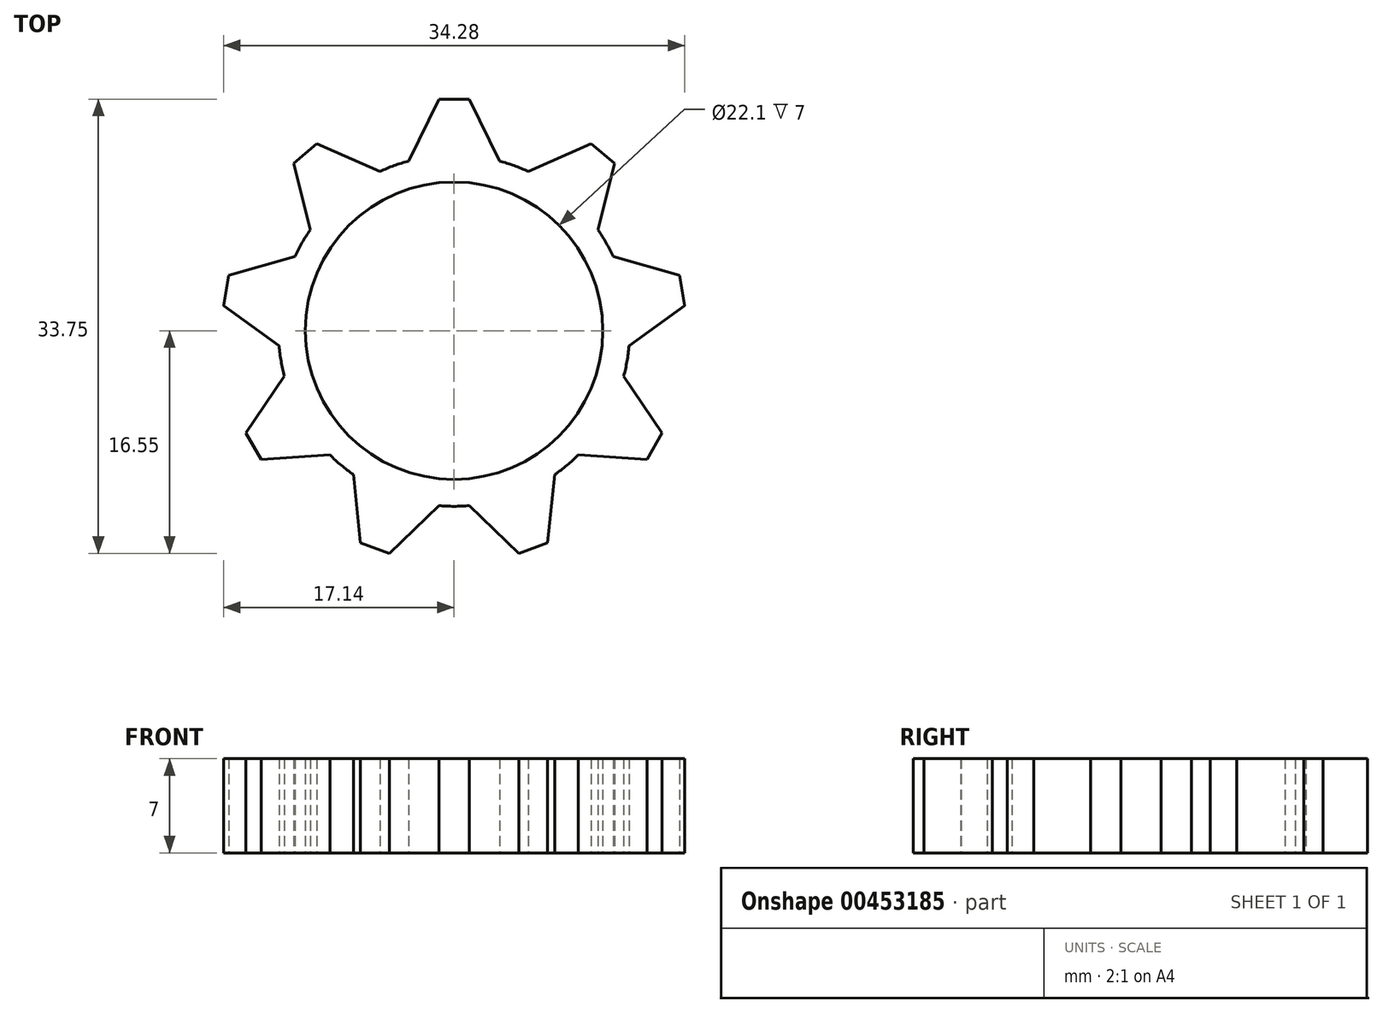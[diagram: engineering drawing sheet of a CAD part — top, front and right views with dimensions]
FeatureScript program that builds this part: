
annotation { "Feature Type Name" : "Feature", "Feature Type Description" : "" }
export const myFeature = defineFeature(function(context is Context, id is Id, definition is map)
    precondition{}
    {
        {
            var Q0;
            Q0=qCreatedBy(makeId("Top.planeOp"),FACE);
            var sketch = newSketch(context, id + "F0", { "sketchPlane" : qUnion([Q0])});
            skCircle(sketch, "E0", {"center": v(0, 0) * mm, "radius": 11.05 * mm});
            skCircle(sketch, "E1.0", {"center": v(0, 0) * mm, "radius": 13.05 * mm});
            skPoint(sketch, "E2.orphan", {"position": v(3.38, 12.6) * mm});
            skPoint(sketch, "E3.MirrorCS.end.orphan", {"position": v(-3.38, 12.6) * mm});
            skPoint(sketch, "E4.1.0", {"position": v(11.37, 6.69) * mm});
            skPoint(sketch, "E4.1.1", {"position": v(6.58, 11.46) * mm});
            skPoint(sketch, "E4.2.0", {"position": v(12.86, -3.14) * mm});
            skPoint(sketch, "E4.2.1", {"position": v(12.83, 3.61) * mm});
            skPoint(sketch, "E4.3.0", {"position": v(6.97, -11.16) * mm});
            skPoint(sketch, "E4.3.1", {"position": v(11.72, -6.35) * mm});
            skPoint(sketch, "E4.4.0", {"position": v(-2.86, -12.68) * mm});
            skPoint(sketch, "E4.4.1", {"position": v(3.9, -12.63) * mm});
            skPoint(sketch, "E4.5.0", {"position": v(-10.9, -6.82) * mm});
            skPoint(sketch, "E4.5.1", {"position": v(-6.08, -11.55) * mm});
            skPoint(sketch, "E4.6.0", {"position": v(-12.45, 3) * mm});
            skPoint(sketch, "E4.6.1", {"position": v(-12.38, -3.75) * mm});
            skPoint(sketch, "E4.7.0", {"position": v(-6.62, 11.06) * mm});
            skPoint(sketch, "E4.7.1", {"position": v(-11.33, 6.22) * mm});
            skPoint(sketch, "E4.center", {"position": v(0.21, -0.02) * mm});
            skLineSegment(sketch, "E5", {"start": v(0, 17.2) * mm, "end": v(1.14, 17.2) * mm});
            skLineSegment(sketch, "E6.MirrorCS", {"start": v(0, 17.2) * mm, "end": v(-1.14, 17.2) * mm});
            skLineSegment(sketch, "E7", {"start": v(-3.38, 12.6) * mm, "end": v(-1.13, 17.2) * mm});
            skLineSegment(sketch, "E8", {"start": v(1.13, 17.2) * mm, "end": v(3.38, 12.6) * mm});
            skLineSegment(sketch, "E9.1.0", {"start": v(-10.19, 13.9) * mm, "end": v(-5.52, 11.83) * mm});
            skLineSegment(sketch, "E9.1.1", {"start": v(-11.06, 13.18) * mm, "end": v(-10.19, 13.9) * mm});
            skLineSegment(sketch, "E9.1.2", {"start": v(-11.06, 13.18) * mm, "end": v(-11.93, 12.45) * mm});
            skLineSegment(sketch, "E9.1.3", {"start": v(-10.69, 7.49) * mm, "end": v(-11.93, 12.45) * mm});
            skLineSegment(sketch, "E9.2.0", {"start": v(-16.74, 4.1) * mm, "end": v(-11.83, 5.52) * mm});
            skLineSegment(sketch, "E9.2.1", {"start": v(-16.94, 2.99) * mm, "end": v(-16.74, 4.1) * mm});
            skLineSegment(sketch, "E9.2.2", {"start": v(-16.94, 2.99) * mm, "end": v(-17.14, 1.87) * mm});
            skLineSegment(sketch, "E9.2.3", {"start": v(-13, -1.14) * mm, "end": v(-17.14, 1.87) * mm});
            skLineSegment(sketch, "E9.3.0", {"start": v(-15.46, -7.62) * mm, "end": v(-12.6, -3.38) * mm});
            skLineSegment(sketch, "E9.3.1", {"start": v(-14.9, -8.6) * mm, "end": v(-15.46, -7.62) * mm});
            skLineSegment(sketch, "E9.3.2", {"start": v(-14.9, -8.6) * mm, "end": v(-14.33, -9.58) * mm});
            skLineSegment(sketch, "E9.3.3", {"start": v(-9.23, -9.23) * mm, "end": v(-14.33, -9.58) * mm});
            skLineSegment(sketch, "E9.4.0", {"start": v(-6.95, -15.77) * mm, "end": v(-7.49, -10.69) * mm});
            skLineSegment(sketch, "E9.4.1", {"start": v(-5.88, -16.16) * mm, "end": v(-6.95, -15.77) * mm});
            skLineSegment(sketch, "E9.4.2", {"start": v(-5.88, -16.16) * mm, "end": v(-4.82, -16.55) * mm});
            skLineSegment(sketch, "E9.4.3", {"start": v(-1.14, -13) * mm, "end": v(-4.82, -16.55) * mm});
            skLineSegment(sketch, "E9.5.0", {"start": v(4.82, -16.55) * mm, "end": v(1.14, -13) * mm});
            skLineSegment(sketch, "E9.5.1", {"start": v(5.88, -16.16) * mm, "end": v(4.82, -16.55) * mm});
            skLineSegment(sketch, "E9.5.2", {"start": v(5.88, -16.16) * mm, "end": v(6.95, -15.77) * mm});
            skLineSegment(sketch, "E9.5.3", {"start": v(7.49, -10.69) * mm, "end": v(6.95, -15.77) * mm});
            skLineSegment(sketch, "E9.6.0", {"start": v(14.33, -9.58) * mm, "end": v(9.23, -9.23) * mm});
            skLineSegment(sketch, "E9.6.1", {"start": v(14.9, -8.6) * mm, "end": v(14.33, -9.58) * mm});
            skLineSegment(sketch, "E9.6.2", {"start": v(14.9, -8.6) * mm, "end": v(15.46, -7.62) * mm});
            skLineSegment(sketch, "E9.6.3", {"start": v(12.6, -3.38) * mm, "end": v(15.46, -7.62) * mm});
            skLineSegment(sketch, "E9.7.0", {"start": v(17.14, 1.87) * mm, "end": v(13, -1.14) * mm});
            skLineSegment(sketch, "E9.7.1", {"start": v(16.94, 2.99) * mm, "end": v(17.14, 1.87) * mm});
            skLineSegment(sketch, "E9.7.2", {"start": v(16.94, 2.99) * mm, "end": v(16.74, 4.1) * mm});
            skLineSegment(sketch, "E9.7.3", {"start": v(11.83, 5.52) * mm, "end": v(16.74, 4.1) * mm});
            skPoint(sketch, "E10.0.8.0", {"position": v(3.2, 12.65) * mm});
            skPoint(sketch, "E10.1.8.0", {"position": v(-3.56, 12.55) * mm});
            skLineSegment(sketch, "E11.2.8.0", {"start": v(11.93, 12.45) * mm, "end": v(10.69, 7.49) * mm});
            skLineSegment(sketch, "E11.3.8.0", {"start": v(11.06, 13.18) * mm, "end": v(11.93, 12.45) * mm});
            skLineSegment(sketch, "E11.6.8.0", {"start": v(11.06, 13.18) * mm, "end": v(10.19, 13.9) * mm});
            skLineSegment(sketch, "E11.9.8.0", {"start": v(5.52, 11.83) * mm, "end": v(10.19, 13.9) * mm});
            skSolve(sketch);
        }
        {
            var Q0;
            Q0=makeQuery(id+"F0.imprint","IMPRINT",FACE,{"disambiguationData":[TD([[makeQuery(id+"F0.imprint","IMPRINT",EDGE,{"derivedFrom":sQuery(id+"F0.wireOp",EDGE,"E5")}),-1.0]])]});
            var Q1;
            Q1=makeQuery(id+"F0.imprint","IMPRINT",FACE,{"disambiguationData":[TD([[makeQuery(id+"F0.imprint","IMPRINT",EDGE,{"derivedFrom":sQuery(id+"F0.wireOp",EDGE,"E0")}),-1.0]])]});
            var Q2;
            {var subQ0=sQuery(id+"F0.wireOp",EDGE,"E11.2.8.0");Q2=makeQuery(id+"F0.imprint","IMPRINT",FACE,{"disambiguationData":[TD([[makeQuery(id+"F0.imprint","IMPRINT",EDGE,{"derivedFrom":subQ0}),-1.0]])]});}
            var Q3;
            {var subQ0=sQuery(id+"F0.wireOp",EDGE,"E9.7.0");Q3=makeQuery(id+"F0.imprint","IMPRINT",FACE,{"disambiguationData":[TD([[makeQuery(id+"F0.imprint","IMPRINT",EDGE,{"derivedFrom":subQ0}),-1.0]])]});}
            var Q4;
            {var subQ0=sQuery(id+"F0.wireOp",EDGE,"E9.6.0");Q4=makeQuery(id+"F0.imprint","IMPRINT",FACE,{"disambiguationData":[TD([[makeQuery(id+"F0.imprint","IMPRINT",EDGE,{"derivedFrom":subQ0}),-1.0]])]});}
            var Q5;
            {var subQ0=sQuery(id+"F0.wireOp",EDGE,"E9.5.0");Q5=makeQuery(id+"F0.imprint","IMPRINT",FACE,{"disambiguationData":[TD([[makeQuery(id+"F0.imprint","IMPRINT",EDGE,{"derivedFrom":subQ0}),-1.0]])]});}
            var Q6;
            {var subQ0=sQuery(id+"F0.wireOp",EDGE,"E9.4.0");Q6=makeQuery(id+"F0.imprint","IMPRINT",FACE,{"disambiguationData":[TD([[makeQuery(id+"F0.imprint","IMPRINT",EDGE,{"derivedFrom":subQ0}),-1.0]])]});}
            var Q7;
            {var subQ0=sQuery(id+"F0.wireOp",EDGE,"E9.3.0");Q7=makeQuery(id+"F0.imprint","IMPRINT",FACE,{"disambiguationData":[TD([[makeQuery(id+"F0.imprint","IMPRINT",EDGE,{"derivedFrom":subQ0}),-1.0]])]});}
            var Q8;
            {var subQ0=sQuery(id+"F0.wireOp",EDGE,"E9.2.0");Q8=makeQuery(id+"F0.imprint","IMPRINT",FACE,{"disambiguationData":[TD([[makeQuery(id+"F0.imprint","IMPRINT",EDGE,{"derivedFrom":subQ0}),-1.0]])]});}
            var Q9;
            {var subQ0=sQuery(id+"F0.wireOp",EDGE,"E9.1.0");Q9=makeQuery(id+"F0.imprint","IMPRINT",FACE,{"disambiguationData":[TD([[makeQuery(id+"F0.imprint","IMPRINT",EDGE,{"derivedFrom":subQ0}),-1.0]])]});}
            extrude(context, id + "F1", {"entities" : qUnion([Q0, Q1, Q2, Q3, Q4, Q5, Q6, Q7, Q8, Q9]), "depth" : 7 * mm});
        }
    });
